# Revit family: BIMLIB_T-образная_трубка_РОСТерм
name_source: partatom
category: Соединительные детали трубопроводов
revit_build: Autodesk Revit 2017 (Build: 20170118_1100(x64)
units: mm (PartAtom-declared; Revit-internal decimal feet)

## family parameters
Всегда вертикально = Нет
На основе рабочей плоскости = Нет
Общий = Нет
При загрузке вырезать с полостями = Нет
Размер круглого соединителя = Использовать диаметр
Тип детали = Тройник

## types (1)
- BIMLIB_T-образная_трубка_РОСТерм
    ADSK_URL документации изделия = http://rostherm.ru
    ADSK_URL страницы изделия = http://rostherm.ru
    ADSK_Версия Revit = 2017
    ADSK_Единица измерения = шт.
    ADSK_Масса = 0
    ADSK_Материал = BIMLIB_Сталь_РТ
    ADSK_Обозначение = ГОСТ 32415-2013
    BL_BIM library = https://bimlib.pro
    URL = http://rostherm.ru
    Изготовитель = РОСТерм
    Ключевая пометка = ﻿﻿  ﻿          ​     ​                                      ﻿       ﻿ ﻿         ​     ​ ﻿                                  ​  ​  ​  ​    ​  ​    ​        ﻿﻿
    Код по классификатору = ﻿﻿  ﻿          ​     ​                                      ﻿       ﻿ ﻿         ​     ​ ﻿                                  ​  ​  ​  ​    ​  ​    ​        ﻿﻿
    Комментарии к типоразмеру = ﻿﻿  ﻿          ​     ​                                      ﻿       ﻿ ﻿         ​     ​ ﻿                                  ​  ​  ​  ​    ​  ​    ​        ﻿﻿
    Описание = Тройник Т-образный для подключения радиатора  ​     ​                                      ﻿       ﻿ ﻿         ​     ​ ﻿                                  ​  ​  ​  ​    ​  ​    ​        ﻿﻿
    РТ_DN2 = 15 мм

## geometry (parser evidence)
native form markers: Sweep x2
no freeform markers — native parametric forms only
